# Revit family: Shower-Shower_Column_Kit-KOHLER-Spaviva-K-EX36244T.rfa_
name_source: partatom
category: Plumbing Fixtures
units: mm (PartAtom-declared; Revit-internal decimal feet)

## family parameters
Cut with Voids When Loaded = No
Host = Face
Maintain Annotation Orientation = No
OmniClass Number = 23.31.17.00
OmniClass Title = Showers
Part Type = Normal
Room Calculation Point = No
Round Connector Dimension = Use Diameter
Shared = No

## types (1)
- CP-Polished Chrome
    ADA Compliant = No
    Assembly Code = D2010700
    CW Connection = Yes
    Cold Water Inlet = Cold Water Inlet
    Date Modified = 07/09/2025
    Default Elevation = 42"
    Description = Modular Column - Basic Version (Low C)
    Drain Included = No
    Finish = Kohler-Metal-CP-Polished_Chrome
    Flow Rate = 3 GPM
    HW Connection = Yes
    Height = 45 11/16"
    Hot Water Inlet = Hot Water Inlet
    Length = 18 9/16"
    Manufacturer = Kohler Co.
    Master Format 2014 = 22 42 23
    Master Format 2014 Name = Residential Showers
    Material = Premium Metal Construction
    Model = K-EX36244T-9-CP
    Nozzle Finish = Kohler-Plastic-0-White
    Pressure = 0.00 psi
    Product Name = Spaviva
    Secondary Finish = Plastic-Pantone-PQ-11-4800-TCX
    Type = 1
    URL = http://www.kohler.com.cn
    Vent Connection = No
    Waste Connection = No
    Waste Water Outlet = Waste Water Outlet
    WaterSense Certified = No
    Width = 23 13/16"

## geometry (parser evidence)
native form markers: Sweep x7
no freeform markers — native parametric forms only
